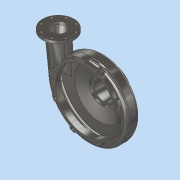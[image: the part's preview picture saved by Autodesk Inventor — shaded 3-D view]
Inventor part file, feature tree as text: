
AUTODESK INVENTOR PART (.ipt)
format: ipt  version: 2019 (Build 230136000, 136)  size: 1,207,296 bytes
history: native  units: mm
features: sketch x20, projected_geometry x14, other x10, hole x6, extrude x5, pattern_circular x4, loft x3, fillet x1
ambient origin geometry x8: Origin, YZ Plane, XZ Plane, XY Plane, X Axis, Y Axis, Z Axis, Center Point
bodies: Solide1 (feature_tree)
feature tree (63):
  other  "Révolution1"
  hole  "Perçage1"  [1 undecoded]
  other  "Axe de construction1"
  pattern_circular  "Réseau circulaire1"  [2 undecoded]
  other  "Plan de construction1"
  extrude  "Extrusion1"  Depth=85.0mm
  extrude  "Extrusion2"  Depth=20.0mm
  hole  "Perçage2"  [1 undecoded]
  pattern_circular  "Réseau circulaire2"  [2 undecoded]
  sketch  "Esquisse6"
  sketch  "Esquisse7"
  sketch  "Esquisse8"
  other  "Plan de construction2"
  sketch  "Esquisse9"
  other  "Plan de construction3"
  loft  "Lissage1"
  fillet  "Congé1"  Radius=216.0mm
  other  "Révolution2"
  sketch  "Esquisse12"
  loft  "Lissage2"
  loft  "Lissage3"
  other  "Révolution3"
  extrude  "Extrusion3"  Depth=25.0mm
  pattern_circular  "Réseau circulaire3"  [2 undecoded]
  extrude  "Extrusion4"  Depth=15.0mm
  hole  "Perçage3"  [1 undecoded]
  pattern_circular  "Réseau circulaire4"  Angle=90.0deg  [1 undecoded]
  other  "Plan de construction4"
  hole  "Perçage4"  [1 undecoded]
  other  "Plan de construction5"
  extrude  "Extrusion5"  Depth=120.75mm
  hole  "Perçage5"  [1 undecoded]
  hole  "Perçage6"  [1 undecoded]
  sketch  "Esquisse1"
  sketch  "Esquisse2"
  sketch  "Esquisse3"
  sketch  "Esquisse4"
  sketch  "Esquisse5"
  sketch  "Esquisse10"
  sketch  "Esquisse11"
  projected_geometry  "Boucle projetée1"
  projected_geometry  "Boucle projetée2"
  projected_geometry  "Boucle projetée3"
  projected_geometry  "Boucle projetée4"
  projected_geometry  "Boucle projetée5"
  projected_geometry  "Boucle projetée6"
  projected_geometry  "Boucle projetée7"
  projected_geometry  "Boucle projetée8"
  sketch  "Esquisse13"
  other  "Arêtes1"
  projected_geometry  "Boucle projetée19"
  projected_geometry  "Boucle projetée20"
  projected_geometry  "Boucle projetée21"
  projected_geometry  "Boucle projetée22"
  projected_geometry  "Boucle projetée23"
  projected_geometry  "Boucle projetée24"
  sketch  "Esquisse15"
  sketch  "Esquisse16"
  sketch  "Esquisse17"
  sketch  "Esquisse18"
  sketch  "Esquisse19"
  sketch  "Esquisse20"
  sketch  "Esquisse21"
note: 13 required parameter values undecoded (feature->parameter linkage not recoverable at this tier; creation-order binding heuristic only, values carry confidence <= 0.55)
